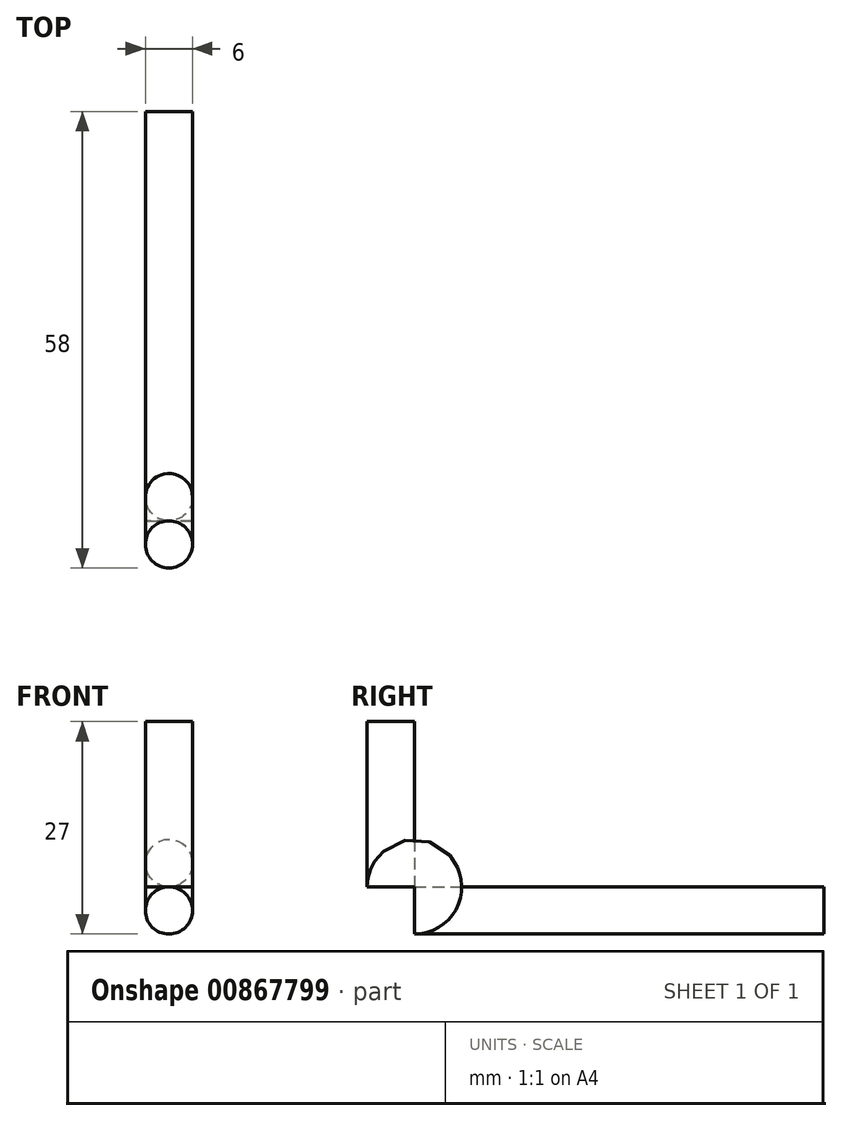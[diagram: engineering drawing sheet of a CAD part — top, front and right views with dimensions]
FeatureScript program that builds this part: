
annotation { "Feature Type Name" : "Feature", "Feature Type Description" : "" }
export const myFeature = defineFeature(function(context is Context, id is Id, definition is map)
    precondition{}
    {
        {
            var Q0;
            Q0=qCreatedBy(makeId("Front.planeOp"),FACE);
            var sketch = newSketch(context, id + "F0", { "sketchPlane" : qUnion([Q0])});
            skCircle(sketch, "E0", {"center": v(0, 0) * mm, "radius": 3 * mm});
            skSolve(sketch);
        }
        {
            var Q0;
            Q0=makeQuery(id+"F0.imprint","IMPRINT",FACE,{"disambiguationData":[TD([[makeQuery(id+"F0.imprint","IMPRINT",EDGE,{"derivedFrom":sQuery(id+"F0.wireOp",EDGE,"E0")}),1.0]])]});
            extrude(context, id + "F1", {"entities" : qUnion([Q0]), "depth" : 52 * mm, "offsetDistance" : 25.4 * mm});
        }
        {
            var Q0;
            Q0=makeQuery(id+"F1.opExtrude","CAP_FACE",FACE,{"disambiguationData":[OSD([sQuery(id+"F0.wireOp",EDGE,"E0")])],"isStart":false});
            var sketch = newSketch(context, id + "F2", { "sketchPlane" : qUnion([Q0])});
            skCircle(sketch, "E1", {"center": v(0, 0) * mm, "radius": 3 * mm});
            skSolve(sketch);
        }
        {
            var Q0;
            Q0=makeQuery(id+"F2.imprint","IMPRINT",FACE,{"disambiguationData":[TD([[makeQuery(id+"F2.imprint","IMPRINT",EDGE,{"derivedFrom":sQuery(id+"F2.wireOp",EDGE,"E1")}),1.0]])]});
            var sketch = newSketch(context, id + "F3", { "sketchPlane" : qUnion([Q0])});
            skLineSegment(sketch, "E2", {"start": v(-49.2, 3) * mm, "end": v(26.38, 3) * mm});
            skSolve(sketch);
        }
        {
            var Q0;
            Q0=makeQuery(id+"F3.imprint","IMPRINT",FACE,{"disambiguationData":[TD([[makeQuery(id+"F3.imprint","IMPRINT",EDGE,{"derivedFrom":makeQuery(id+"F2.imprint","IMPRINT",EDGE,{"derivedFrom":sQuery(id+"F2.wireOp",EDGE,"E1")})}),1.0]])]});
            var Q1;
            Q1=sQuery(id+"F3.wireOp",EDGE,"E2");
            revolve(context, id + "F4", {"operationType" : NewBodyOperationType.ADD, "surfaceOperationType" : NewSurfaceOperationType.NEW, "entities" : qUnion([Q0]), "axis" : qUnion([Q1]), "revolveType" : RevolveType.ONE_DIRECTION, "oppositeDirection" : true, "angle" : 90 * degree});
        }
        {
            var Q0;
            Q0=makeQuery(id+"F4.opRevolve","CAP_FACE",FACE,{"disambiguationData":[OSD([sQuery(id+"F2.wireOp",EDGE,"E1")])],"isStart":false});
            var sketch = newSketch(context, id + "F5", { "sketchPlane" : qUnion([Q0])});
            skCircle(sketch, "E3", {"center": v(0, -55) * mm, "radius": 3 * mm});
            skSolve(sketch);
        }
        {
            var Q0;
            Q0=makeQuery(id+"F5.imprint","IMPRINT",FACE,{"disambiguationData":[TD([[makeQuery(id+"F5.imprint","IMPRINT",EDGE,{"derivedFrom":sQuery(id+"F5.wireOp",EDGE,"E3")}),1.0]])]});
            extrude(context, id + "F6", {"entities" : qUnion([Q0]), "operationType" : NewBodyOperationType.ADD, "depth" : 21 * mm, "offsetDistance" : 25.4 * mm});
        }
    });
